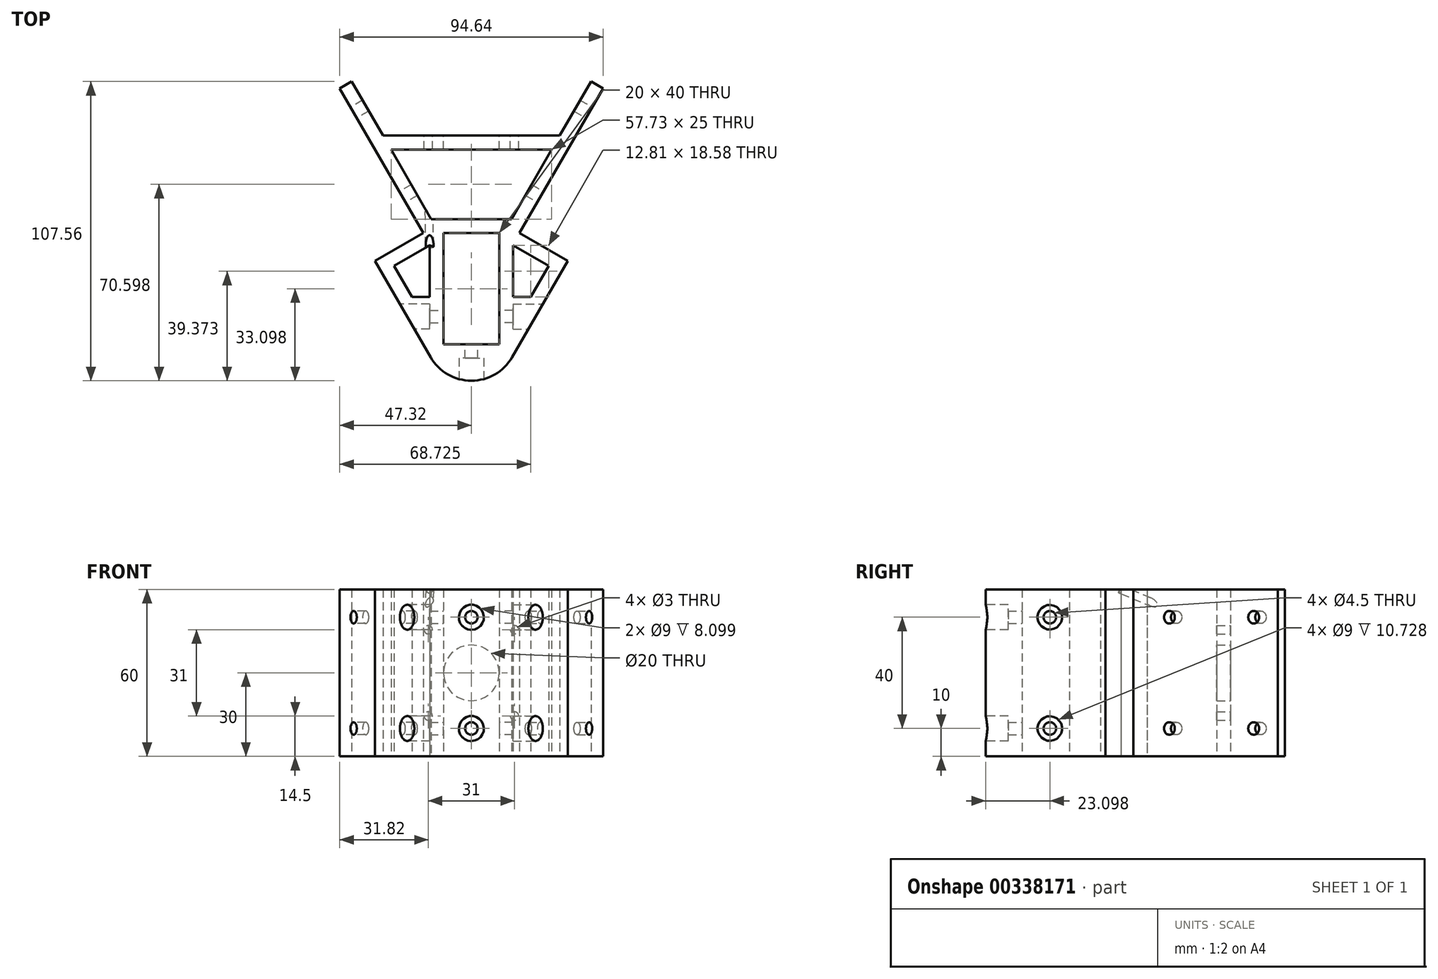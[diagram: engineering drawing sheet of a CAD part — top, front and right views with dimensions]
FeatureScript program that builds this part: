
annotation { "Feature Type Name" : "Feature", "Feature Type Description" : "" }
export const myFeature = defineFeature(function(context is Context, id is Id, definition is map)
    precondition{}
    {
        {
            var Q0;
            Q0=qCreatedBy(makeId("Top.planeOp"),FACE);
            var sketch = newSketch(context, id + "F0", { "sketchPlane" : qUnion([Q0])});
            skLineSegment(sketch, "E0", {"start": v(14.43, 6.05) * mm, "end": v(28.87, 31.05) * mm});
            skLineSegment(sketch, "E1", {"start": v(43, 55.5) * mm, "end": v(47.32, 53) * mm});
            skLineSegment(sketch, "E2", {"start": v(47.32, 53) * mm, "end": v(17.32, 1.05) * mm});
            skLineSegment(sketch, "E3.bottom", {"start": v(10, -38.95) * mm, "end": v(-10, -38.95) * mm});
            skLineSegment(sketch, "E3.top", {"start": v(10, 1.05) * mm, "end": v(-10, 1.05) * mm});
            skLineSegment(sketch, "E3.left", {"start": v(10, -38.95) * mm, "end": v(10, 1.05) * mm});
            skLineSegment(sketch, "E3.right", {"start": v(-10, -38.95) * mm, "end": v(-10, 1.05) * mm});
            skPoint(sketch, "E3.middle", {"position": v(0, -18.95) * mm});
            skLineSegment(sketch, "E4", {"start": v(17.32, 1.05) * mm, "end": v(34.64, -8.95) * mm});
            skLineSegment(sketch, "E5", {"start": v(34.64, -8.95) * mm, "end": v(14.64, -43.6) * mm});
            skPoint(sketch, "E6.orphan", {"position": v(0, -28.95) * mm});
            skLineSegment(sketch, "E7", {"start": v(-14.43, 6.05) * mm, "end": v(-28.87, 31.05) * mm});
            skLineSegment(sketch, "E8", {"start": v(-43, 55.5) * mm, "end": v(-47.32, 53) * mm});
            skLineSegment(sketch, "E9", {"start": v(-47.32, 53) * mm, "end": v(-17.32, 1.05) * mm});
            skLineSegment(sketch, "E10", {"start": v(-17.32, 1.05) * mm, "end": v(-34.64, -8.95) * mm});
            skLineSegment(sketch, "E11", {"start": v(-34.64, -8.95) * mm, "end": v(-14.64, -43.6) * mm});
            skArc(sketch, "E12", {"start": v(-14.64, -43.6) * mm, "mid": v(0, -52.05) * mm, "end": v(14.64, -43.6) * mm});
            skLineSegment(sketch, "E13", {"start": v(-14.43, 6.05) * mm, "end": v(14.43, 6.05) * mm});
            skLineSegment(sketch, "E14", {"start": v(-28.87, 31.05) * mm, "end": v(28.87, 31.05) * mm});
            skLineSegment(sketch, "E15", {"start": v(-31.75, 36.05) * mm, "end": v(31.75, 36.05) * mm});
            skLineSegment(sketch, "E16.trimOffspring", {"start": v(-31.75, 36.05) * mm, "end": v(-43, 55.5) * mm});
            skLineSegment(sketch, "E17.trimOffspring", {"start": v(31.75, 36.05) * mm, "end": v(43, 55.5) * mm});
            skLineSegment(sketch, "E18", {"start": v(15, -4.47) * mm, "end": v(15, -21.97) * mm});
            skLineSegment(sketch, "E19", {"start": v(15, -21.97) * mm, "end": v(21.35, -21.97) * mm});
            skLineSegment(sketch, "E20", {"start": v(21.35, -21.97) * mm, "end": v(27.81, -10.78) * mm});
            skLineSegment(sketch, "E21", {"start": v(27.81, -10.78) * mm, "end": v(15, -3.39) * mm});
            skLineSegment(sketch, "E22", {"start": v(15, -3.39) * mm, "end": v(15, -4.47) * mm});
            skLineSegment(sketch, "E23", {"start": v(-15, -9.7) * mm, "end": v(-15, -21.97) * mm});
            skLineSegment(sketch, "E24", {"start": v(-15, -21.97) * mm, "end": v(-21.35, -21.97) * mm});
            skLineSegment(sketch, "E25", {"start": v(-21.35, -21.97) * mm, "end": v(-27.81, -10.78) * mm});
            skLineSegment(sketch, "E26", {"start": v(-27.81, -10.78) * mm, "end": v(-15, -3.39) * mm});
            skLineSegment(sketch, "E27", {"start": v(-15, -3.39) * mm, "end": v(-15, -9.7) * mm});
            skSolve(sketch);
        }
        {
            var Q0;
            Q0=makeQuery(id+"F0.imprint","IMPRINT",FACE,{"disambiguationData":[TD([[makeQuery(id+"F0.imprint","IMPRINT",EDGE,{"derivedFrom":sQuery(id+"F0.wireOp",EDGE,"E0")}),-1.0]])]});
            extrude(context, id + "F1", {"entities" : qUnion([Q0]), "depth" : 60 * mm});
        }
        {
            var Q0;
            Q0=makeQuery(id+"F1.opExtrude","SWEPT_FACE",FACE,{"disambiguationData":[OSD([sQuery(id+"F0.wireOp",EDGE,"E15")])]});
            var sketch = newSketch(context, id + "F2", { "sketchPlane" : qUnion([Q0])});
            skPoint(sketch, "E28.middle", {"position": v(0, 30) * mm});
            skPoint(sketch, "E28.middle.positionSnap0", {"position": v(31.75, 30) * mm});
            skPoint(sketch, "E28.centerSnap0", {"position": v(31.75, 30) * mm});
            skCircle(sketch, "E29", {"center": v(-15.5, 45.5) * mm, "radius": 1.5 * mm});
            skCircle(sketch, "E30", {"center": v(15.5, 45.5) * mm, "radius": 1.5 * mm});
            skCircle(sketch, "E31", {"center": v(15.5, 14.5) * mm, "radius": 1.5 * mm});
            skCircle(sketch, "E32", {"center": v(-15.5, 14.5) * mm, "radius": 1.5 * mm});
            skCircle(sketch, "E33", {"center": v(0, 30) * mm, "radius": 10 * mm});
            skSolve(sketch);
        }
        {
            var Q0;
            Q0=makeQuery(id+"F2.imprint","IMPRINT",FACE,{"disambiguationData":[TD([[makeQuery(id+"F2.imprint","IMPRINT",EDGE,{"derivedFrom":sQuery(id+"F2.wireOp",EDGE,"E29")}),1.0]])]});
            var Q1;
            Q1=makeQuery(id+"F2.imprint","IMPRINT",FACE,{"disambiguationData":[TD([[makeQuery(id+"F2.imprint","IMPRINT",EDGE,{"derivedFrom":sQuery(id+"F2.wireOp",EDGE,"E30")}),1.0]])]});
            var Q2;
            Q2=makeQuery(id+"F2.imprint","IMPRINT",FACE,{"disambiguationData":[TD([[makeQuery(id+"F2.imprint","IMPRINT",EDGE,{"derivedFrom":sQuery(id+"F2.wireOp",EDGE,"E31")}),1.0]])]});
            var Q3;
            Q3=makeQuery(id+"F2.imprint","IMPRINT",FACE,{"disambiguationData":[TD([[makeQuery(id+"F2.imprint","IMPRINT",EDGE,{"derivedFrom":sQuery(id+"F2.wireOp",EDGE,"E32")}),1.0]])]});
            var Q4;
            Q4=makeQuery(id+"F2.imprint","IMPRINT",FACE,{"disambiguationData":[TD([[makeQuery(id+"F2.imprint","IMPRINT",EDGE,{"derivedFrom":sQuery(id+"F2.wireOp",EDGE,"E33")}),1.0]])]});
            extrude(context, id + "F3", {"entities" : qUnion([Q0, Q1, Q2, Q3, Q4]), "operationType" : NewBodyOperationType.REMOVE, "oppositeDirection" : true, "depth" : 6 * mm});
        }
        {
            var Q0;
            Q0=makeQuery(id+"F1.opExtrude","SWEPT_FACE",FACE,{"disambiguationData":[OSD([sQuery(id+"F0.wireOp",EDGE,"E9")])]});
            var sketch = newSketch(context, id + "F4", { "sketchPlane" : qUnion([Q0])});
            skCircle(sketch, "E34", {"center": v(-59.57, 50) * mm, "radius": 2.25 * mm});
            skCircle(sketch, "E35", {"center": v(-24.57, 50) * mm, "radius": 2.25 * mm});
            skCircle(sketch, "E36", {"center": v(-24.57, 10) * mm, "radius": 2.25 * mm});
            skCircle(sketch, "E37", {"center": v(-59.57, 10) * mm, "radius": 2.25 * mm});
            skPoint(sketch, "E38.start.orphan", {"position": v(-9.57, 50) * mm});
            skSolve(sketch);
        }
        {
            var Q0;
            Q0=makeQuery(id+"F4.imprint","IMPRINT",FACE,{"disambiguationData":[TD([[makeQuery(id+"F4.imprint","IMPRINT",EDGE,{"derivedFrom":sQuery(id+"F4.wireOp",EDGE,"E35")}),1.0]])]});
            var Q1;
            Q1=makeQuery(id+"F4.imprint","IMPRINT",FACE,{"disambiguationData":[TD([[makeQuery(id+"F4.imprint","IMPRINT",EDGE,{"derivedFrom":sQuery(id+"F4.wireOp",EDGE,"E34")}),1.0]])]});
            var Q2;
            Q2=makeQuery(id+"F4.imprint","IMPRINT",FACE,{"disambiguationData":[TD([[makeQuery(id+"F4.imprint","IMPRINT",EDGE,{"derivedFrom":sQuery(id+"F4.wireOp",EDGE,"E37")}),1.0]])]});
            var Q3;
            Q3=makeQuery(id+"F4.imprint","IMPRINT",FACE,{"disambiguationData":[TD([[makeQuery(id+"F4.imprint","IMPRINT",EDGE,{"derivedFrom":sQuery(id+"F4.wireOp",EDGE,"E36")}),1.0]])]});
            extrude(context, id + "F5", {"entities" : qUnion([Q0, Q1, Q2, Q3]), "operationType" : NewBodyOperationType.REMOVE, "oppositeDirection" : true, "depth" : 6 * mm});
        }
        {
            var Q0;
            Q0=makeQuery(id+"F1.opExtrude","SWEPT_FACE",FACE,{"disambiguationData":[OSD([sQuery(id+"F0.wireOp",EDGE,"E2")])]});
            var sketch = newSketch(context, id + "F6", { "sketchPlane" : qUnion([Q0])});
            skCircle(sketch, "E39", {"center": v(24.57, 50) * mm, "radius": 2.25 * mm});
            skCircle(sketch, "E40", {"center": v(59.57, 50) * mm, "radius": 2.25 * mm});
            skCircle(sketch, "E41", {"center": v(59.57, 10) * mm, "radius": 2.25 * mm});
            skCircle(sketch, "E42", {"center": v(24.57, 10) * mm, "radius": 2.25 * mm});
            skSolve(sketch);
        }
        {
            var Q0;
            Q0=makeQuery(id+"F6.imprint","IMPRINT",FACE,{"disambiguationData":[TD([[makeQuery(id+"F6.imprint","IMPRINT",EDGE,{"derivedFrom":sQuery(id+"F6.wireOp",EDGE,"E39")}),1.0]])]});
            var Q1;
            Q1=makeQuery(id+"F6.imprint","IMPRINT",FACE,{"disambiguationData":[TD([[makeQuery(id+"F6.imprint","IMPRINT",EDGE,{"derivedFrom":sQuery(id+"F6.wireOp",EDGE,"E40")}),1.0]])]});
            var Q2;
            Q2=makeQuery(id+"F6.imprint","IMPRINT",FACE,{"disambiguationData":[TD([[makeQuery(id+"F6.imprint","IMPRINT",EDGE,{"derivedFrom":sQuery(id+"F6.wireOp",EDGE,"E41")}),1.0]])]});
            var Q3;
            Q3=makeQuery(id+"F6.imprint","IMPRINT",FACE,{"disambiguationData":[TD([[makeQuery(id+"F6.imprint","IMPRINT",EDGE,{"derivedFrom":sQuery(id+"F6.wireOp",EDGE,"E42")}),1.0]])]});
            extrude(context, id + "F7", {"entities" : qUnion([Q0, Q1, Q2, Q3]), "operationType" : NewBodyOperationType.REMOVE, "oppositeDirection" : true, "depth" : 6 * mm});
        }
        {
            var Q0;
            Q0=makeQuery(id+"F1.opExtrude","SWEPT_FACE",FACE,{"disambiguationData":[OSD([sQuery(id+"F0.wireOp",EDGE,"E3.bottom")])]});
            var sketch = newSketch(context, id + "F8", { "sketchPlane" : qUnion([Q0])});
            skCircle(sketch, "E43", {"center": v(0, 10) * mm, "radius": 2.25 * mm});
            skCircle(sketch, "E44", {"center": v(0, 50) * mm, "radius": 2.25 * mm});
            skCircle(sketch, "E45", {"center": v(0, 50) * mm, "radius": 4.5 * mm});
            skCircle(sketch, "E46", {"center": v(0, 10) * mm, "radius": 4.5 * mm});
            skLineSegment(sketch, "E47.trimOffspring", {"start": v(0, 14.5) * mm, "end": v(0, 12.25) * mm});
            skPoint(sketch, "E48.start.orphan", {"position": v(0, 60) * mm});
            skPoint(sketch, "E49.trimOffspring.end.orphan", {"position": v(0, 0) * mm});
            skSolve(sketch);
        }
        {
            var Q0;
            Q0=makeQuery(id+"F1.opExtrude","SWEPT_FACE",FACE,{"disambiguationData":[OSD([sQuery(id+"F0.wireOp",EDGE,"E3.right")])]});
            var sketch = newSketch(context, id + "F9", { "sketchPlane" : qUnion([Q0])});
            skCircle(sketch, "E50", {"center": v(-28.95, 50) * mm, "radius": 2.25 * mm});
            skCircle(sketch, "E51", {"center": v(-28.95, 10) * mm, "radius": 2.25 * mm});
            skCircle(sketch, "E52", {"center": v(-28.95, 50) * mm, "radius": 4.5 * mm});
            skCircle(sketch, "E53", {"center": v(-28.95, 10) * mm, "radius": 4.5 * mm});
            skPoint(sketch, "E54.start.orphan", {"position": v(-28.95, 60) * mm});
            skPoint(sketch, "E55.orphan", {"position": v(-28.95, 0) * mm});
            skSolve(sketch);
        }
        {
            var Q0;
            Q0=makeQuery(id+"F1.opExtrude","SWEPT_FACE",FACE,{"disambiguationData":[OSD([sQuery(id+"F0.wireOp",EDGE,"E3.left")])]});
            var sketch = newSketch(context, id + "F10", { "sketchPlane" : qUnion([Q0])});
            skCircle(sketch, "E56", {"center": v(28.95, 50) * mm, "radius": 2.25 * mm});
            skCircle(sketch, "E57", {"center": v(28.95, 10) * mm, "radius": 2.25 * mm});
            skCircle(sketch, "E58", {"center": v(28.95, 50) * mm, "radius": 4.5 * mm});
            skCircle(sketch, "E59", {"center": v(28.95, 10) * mm, "radius": 4.5 * mm});
            skPoint(sketch, "E60.start.orphan", {"position": v(28.95, 60) * mm});
            skPoint(sketch, "E61.orphan", {"position": v(28.95, 0) * mm});
            skSolve(sketch);
        }
        {
            var Q0;
            Q0=makeQuery(id+"F9.imprint","IMPRINT",FACE,{"disambiguationData":[TD([[makeQuery(id+"F9.imprint","IMPRINT",EDGE,{"derivedFrom":sQuery(id+"F9.wireOp",EDGE,"E50")}),-1.0]])]});
            var Q1;
            Q1=makeQuery(id+"F9.imprint","IMPRINT",FACE,{"disambiguationData":[TD([[makeQuery(id+"F9.imprint","IMPRINT",EDGE,{"derivedFrom":sQuery(id+"F9.wireOp",EDGE,"E51")}),-1.0]])]});
            extrude(context, id + "F11", {"entities" : qUnion([Q0, Q1]), "operationType" : NewBodyOperationType.ADD, "depth" : -20 * mm});
        }
        {
            var Q0;
            Q0=makeQuery(id+"F10.imprint","IMPRINT",FACE,{"disambiguationData":[TD([[makeQuery(id+"F10.imprint","IMPRINT",EDGE,{"derivedFrom":sQuery(id+"F10.wireOp",EDGE,"E57")}),-1.0]])]});
            var Q1;
            Q1=makeQuery(id+"F10.imprint","IMPRINT",FACE,{"disambiguationData":[TD([[makeQuery(id+"F10.imprint","IMPRINT",EDGE,{"derivedFrom":sQuery(id+"F10.wireOp",EDGE,"E56")}),-1.0]])]});
            extrude(context, id + "F12", {"entities" : qUnion([Q0, Q1]), "operationType" : NewBodyOperationType.ADD, "depth" : -20 * mm});
        }
        {
            var Q0;
            Q0=makeQuery(id+"F8.imprint","IMPRINT",FACE,{"disambiguationData":[TD([[makeQuery(id+"F8.imprint","IMPRINT",EDGE,{"derivedFrom":sQuery(id+"F8.wireOp",EDGE,"E44")}),-1.0]])]});
            var Q1;
            Q1=makeQuery(id+"F8.imprint","IMPRINT",FACE,{"disambiguationData":[TD([[makeQuery(id+"F8.imprint","IMPRINT",EDGE,{"derivedFrom":sQuery(id+"F8.wireOp",EDGE,"E43")}),-1.0]])]});
            extrude(context, id + "F13", {"entities" : qUnion([Q0, Q1]), "operationType" : NewBodyOperationType.ADD, "depth" : -20 * mm});
        }
        {
            var Q0;
            Q0=makeQuery(id+"F10.imprint","IMPRINT",FACE,{"disambiguationData":[TD([[makeQuery(id+"F10.imprint","IMPRINT",EDGE,{"derivedFrom":sQuery(id+"F10.wireOp",EDGE,"E57")}),1.0]])]});
            var Q1;
            Q1=makeQuery(id+"F10.imprint","IMPRINT",FACE,{"disambiguationData":[TD([[makeQuery(id+"F10.imprint","IMPRINT",EDGE,{"derivedFrom":sQuery(id+"F10.wireOp",EDGE,"E56")}),1.0]])]});
            extrude(context, id + "F14", {"entities" : qUnion([Q0, Q1]), "operationType" : NewBodyOperationType.REMOVE, "oppositeDirection" : true, "depth" : 25 * mm});
        }
        {
            var Q0;
            Q0=makeQuery(id+"F9.imprint","IMPRINT",FACE,{"disambiguationData":[TD([[makeQuery(id+"F9.imprint","IMPRINT",EDGE,{"derivedFrom":sQuery(id+"F9.wireOp",EDGE,"E50")}),1.0]])]});
            var Q1;
            Q1=makeQuery(id+"F9.imprint","IMPRINT",FACE,{"disambiguationData":[TD([[makeQuery(id+"F9.imprint","IMPRINT",EDGE,{"derivedFrom":sQuery(id+"F9.wireOp",EDGE,"E51")}),1.0]])]});
            extrude(context, id + "F15", {"entities" : qUnion([Q0, Q1]), "operationType" : NewBodyOperationType.REMOVE, "oppositeDirection" : true, "depth" : 25 * mm});
        }
        {
            var Q0;
            Q0=makeQuery(id+"F8.imprint","IMPRINT",FACE,{"disambiguationData":[TD([[makeQuery(id+"F8.imprint","IMPRINT",EDGE,{"derivedFrom":sQuery(id+"F8.wireOp",EDGE,"E44")}),1.0]])]});
            var Q1;
            Q1=makeQuery(id+"F8.imprint","IMPRINT",FACE,{"disambiguationData":[TD([[makeQuery(id+"F8.imprint","IMPRINT",EDGE,{"derivedFrom":sQuery(id+"F8.wireOp",EDGE,"E43")}),1.0]])]});
            extrude(context, id + "F16", {"entities" : qUnion([Q0, Q1]), "operationType" : NewBodyOperationType.REMOVE, "oppositeDirection" : true, "depth" : 25 * mm});
        }
        {
            var Q0;
            Q0=makeQuery(id+"F13.opExtrude","CAP_FACE",FACE,{"disambiguationData":[OSD([sQuery(id+"F8.wireOp",EDGE,"E43"),sQuery(id+"F8.wireOp",EDGE,"E46")])],"isStart":false});
            var Q1;
            Q1=makeQuery(id+"F13.opExtrude","CAP_FACE",FACE,{"disambiguationData":[OSD([sQuery(id+"F8.wireOp",EDGE,"E44"),sQuery(id+"F8.wireOp",EDGE,"E45")])],"isStart":false});
            extrude(context, id + "F17", {"entities" : qUnion([Q0, Q1]), "operationType" : NewBodyOperationType.REMOVE, "oppositeDirection" : true, "depth" : 15 * mm});
        }
        {
            var Q0;
            Q0=makeQuery(id+"F12.opExtrude","CAP_FACE",FACE,{"disambiguationData":[OSD([sQuery(id+"F10.wireOp",EDGE,"E56"),sQuery(id+"F10.wireOp",EDGE,"E58")])],"isStart":false});
            var Q1;
            Q1=makeQuery(id+"F12.opExtrude","CAP_FACE",FACE,{"disambiguationData":[OSD([sQuery(id+"F10.wireOp",EDGE,"E57"),sQuery(id+"F10.wireOp",EDGE,"E59")])],"isStart":false});
            extrude(context, id + "F18", {"entities" : qUnion([Q0, Q1]), "operationType" : NewBodyOperationType.REMOVE, "oppositeDirection" : true, "depth" : 15 * mm});
        }
        {
            var Q0;
            Q0=makeQuery(id+"F11.opExtrude","CAP_FACE",FACE,{"disambiguationData":[OSD([sQuery(id+"F9.wireOp",EDGE,"E51"),sQuery(id+"F9.wireOp",EDGE,"E53")])],"isStart":false});
            var Q1;
            Q1=makeQuery(id+"F11.opExtrude","CAP_FACE",FACE,{"disambiguationData":[OSD([sQuery(id+"F9.wireOp",EDGE,"E50"),sQuery(id+"F9.wireOp",EDGE,"E52")])],"isStart":false});
            extrude(context, id + "F19", {"entities" : qUnion([Q0, Q1]), "operationType" : NewBodyOperationType.REMOVE, "oppositeDirection" : true, "depth" : 15 * mm});
        }
        {
            var Q0;
            Q0=makeQuery(id+"F1.opExtrude","SWEPT_FACE",FACE,{"disambiguationData":[OSD([sQuery(id+"F0.wireOp",EDGE,"E14")])]});
            var sketch = newSketch(context, id + "F20", { "sketchPlane" : qUnion([Q0])});
            skPoint(sketch, "E62", {"position": v(-15.5, 45.5) * mm});
            skPoint(sketch, "E63", {"position": v(-15.5, 14.5) * mm});
            skSolve(sketch);
        }
        {
            var Q0;
            Q0=sQuery(id+"F20.wireOp",VERTEX,"E62");
            var Q1;
            Q1=sQuery(id+"F20.wireOp",VERTEX,"E63");
            var Q2;
            Q2=makeQuery(id+"F1.opExtrude","CAP_VERTEX",VERTEX,{"disambiguationData":[OSD([sQuery(id+"F0.wireOp",EDGE,"E26"),sQuery(id+"F0.wireOp",EDGE,"E27")])],"isStart":false});
            cPlane(context, id + "F21", {"entities" : qUnion([Q0, Q1, Q2]), "cplaneType" : CPlaneType.THREE_POINT, "offset" : 25 * mm, "width" : 150 * mm, "height" : 150 * mm});
        }
        {
            var Q0;
            Q0=qCreatedBy(id+"F21.planeOp",FACE);
            var sketch = newSketch(context, id + "F22", { "sketchPlane" : qUnion([Q0])});
            skLineSegment(sketch, "E64", {"start": v(-3.17, 60) * mm, "end": v(31.26, 45.51) * mm});
            skLineSegment(sketch, "E65", {"start": v(-3.07, 0) * mm, "end": v(31.26, 14.5) * mm});
            skLineSegment(sketch, "E66", {"start": v(31.26, 13) * mm, "end": v(-3.08, -1.5) * mm});
            skLineSegment(sketch, "E67", {"start": v(-3.08, -1.5) * mm, "end": v(-3.07, 0) * mm});
            skLineSegment(sketch, "E68", {"start": v(31.26, 14.5) * mm, "end": v(31.26, 13) * mm});
            skLineSegment(sketch, "E69", {"start": v(31.26, 47.04) * mm, "end": v(31.26, 45.51) * mm});
            skLineSegment(sketch, "E70", {"start": v(31.26, 47.04) * mm, "end": v(-3.07, 61.5) * mm});
            skLineSegment(sketch, "E71", {"start": v(-3.07, 61.5) * mm, "end": v(-3.17, 60) * mm});
            skSolve(sketch);
        }
        {
            var Q0;
            Q0=makeQuery(id+"F22.imprint","IMPRINT",FACE,{"disambiguationData":[TD([[makeQuery(id+"F22.imprint","IMPRINT",EDGE,{"derivedFrom":sQuery(id+"F22.wireOp",EDGE,"E64")}),1.0]])]});
            var Q1;
            Q1=sQuery(id+"F22.wireOp",EDGE,"E64");
            revolve(context, id + "F23", {"operationType" : NewBodyOperationType.REMOVE, "entities" : qUnion([Q0]), "axis" : qUnion([Q1]), "revolveType" : RevolveType.FULL, "oppositeDirection" : true});
        }
    });
